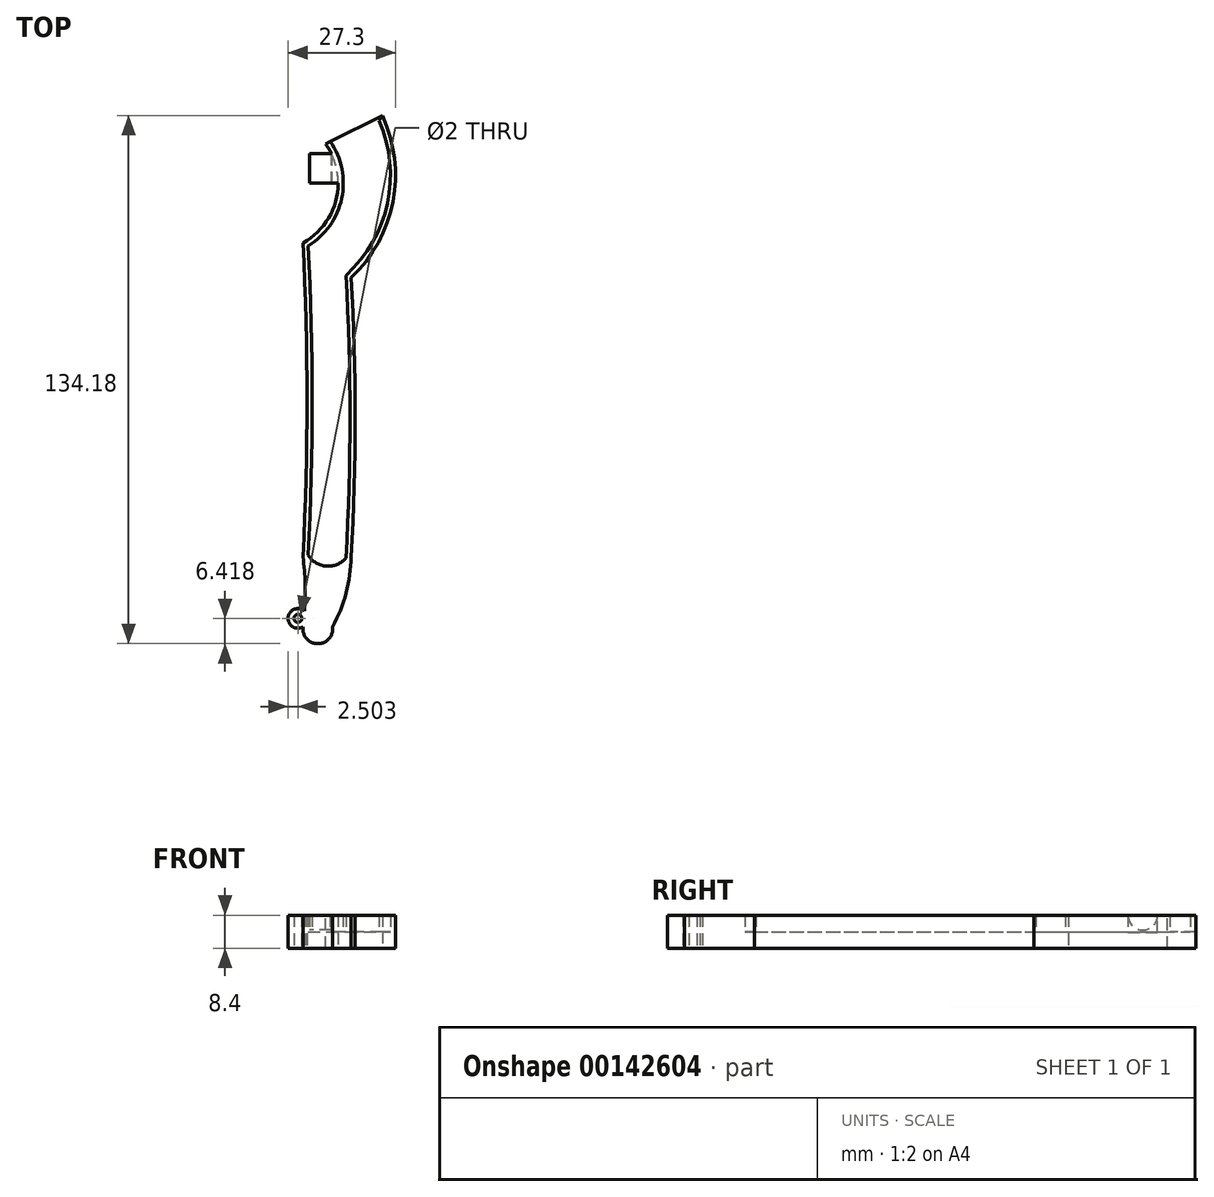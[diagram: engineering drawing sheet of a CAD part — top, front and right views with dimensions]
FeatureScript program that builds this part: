
annotation { "Feature Type Name" : "Feature", "Feature Type Description" : "" }
export const myFeature = defineFeature(function(context is Context, id is Id, definition is map)
    precondition{}
    {
        {
            var Q0;
            Q0=qCreatedBy(makeId("Top.planeOp"),FACE);
            var sketch = newSketch(context, id + "F0", { "sketchPlane" : qUnion([Q0])});
            skArc(sketch, "E0", {"start": v(-18, -31.8) * mm, "mid": v(-9.08, -15.9) * mm, "end": v(-18, 0) * mm});
            skArc(sketch, "E1", {"start": v(-8.38, -39.3) * mm, "mid": v(2.12, -21) * mm, "end": v(0, 0) * mm});
            skArc(sketch, "E2", {"start": v(-18, -110.4) * mm, "mid": v(-17, -71.1) * mm, "end": v(-18, -31.8) * mm});
            skArc(sketch, "E3", {"start": v(-8.38, -111.1) * mm, "mid": v(-7.37, -75.2) * mm, "end": v(-8.38, -39.3) * mm});
            skArc(sketch, "E4", {"start": v(-18, -110.4) * mm, "mid": v(-13.37, -113.18) * mm, "end": v(-8.38, -111.1) * mm});
            skLineSegment(sketch, "E5", {"start": v(0, 0) * mm, "end": v(-18, 0) * mm});
            skArc(sketch, "E6.0", {"start": v(-19.32, -110.8) * mm, "mid": v(-18.3, -70.94) * mm, "end": v(-19.34, -31.07) * mm});
            skLineSegment(sketch, "E6.1", {"start": v(0.84, 1.3) * mm, "end": v(-25.59, 1.3) * mm});
            skArc(sketch, "E6.2", {"start": v(-7.05, -39.84) * mm, "mid": v(3.54, -20.54) * mm, "end": v(0.84, 1.3) * mm});
            skArc(sketch, "E6.3", {"start": v(-19.34, -31.07) * mm, "mid": v(-10.7, -12.62) * mm, "end": v(-25.59, 1.3) * mm});
            skArc(sketch, "E6.4", {"start": v(-7.06, -110.8) * mm, "mid": v(-6.07, -75.32) * mm, "end": v(-7.05, -39.84) * mm});
            skArc(sketch, "E7", {"start": v(-19.32, -128.6) * mm, "mid": v(-18.75, -119.7) * mm, "end": v(-19.32, -110.8) * mm});
            skArc(sketch, "E8", {"start": v(-11.78, -128.6) * mm, "mid": v(-8.38, -119.98) * mm, "end": v(-7.06, -110.8) * mm});
            skArc(sketch, "E9", {"start": v(-19.32, -128.6) * mm, "mid": v(-15.55, -132.88) * mm, "end": v(-11.78, -128.6) * mm});
            skArc(sketch, "E10", {"start": v(-18.93, -124.62) * mm, "mid": v(-23.1, -126.21) * mm, "end": v(-19.32, -128.6) * mm});
            skCircle(sketch, "E11", {"center": v(-20.62, -126.46) * mm, "radius": 1 * mm});
            skLineSegment(sketch, "E12", {"start": v(-10.38, -15.9) * mm, "end": v(-17.68, -15.9) * mm});
            skLineSegment(sketch, "E13", {"start": v(-17.68, -15.9) * mm, "end": v(-17.68, -8.4) * mm});
            skLineSegment(sketch, "E14", {"start": v(-17.68, -8.4) * mm, "end": v(-12.09, -8.4) * mm});
            skSolve(sketch);
        }
        {
            var Q0;
            Q0=makeQuery(id+"F0.imprint","IMPRINT",FACE,{"disambiguationData":[TD([[makeQuery(id+"F0.imprint","IMPRINT",EDGE,{"derivedFrom":sQuery(id+"F0.wireOp",EDGE,"E0")}),1.0]])]});
            var Q1;
            {var subQ0=sQuery(id+"F0.wireOp",EDGE,"E10");Q1=makeQuery(id+"F0.imprint","IMPRINT",FACE,{"disambiguationData":[TD([[makeQuery(id+"F0.imprint","IMPRINT",EDGE,{"derivedFrom":subQ0}),1.0]])]});}
            extrude(context, id + "F1", {"entities" : qUnion([Q0, Q1]), "depth" : 8.4 * mm});
        }
        {
            var Q0;
            Q0=makeQuery(id+"F0.imprint","IMPRINT",FACE,{"disambiguationData":[TD([[makeQuery(id+"F0.imprint","IMPRINT",EDGE,{"derivedFrom":sQuery(id+"F0.wireOp",EDGE,"E0")}),-1.0]])]});
            extrude(context, id + "F2", {"entities" : qUnion([Q0]), "operationType" : NewBodyOperationType.ADD, "depth" : 4.2 * mm});
        }
        {
            var Q0;
            {var subQ0=sQuery(id+"F0.wireOp",EDGE,"E12");Q0=makeQuery(id+"F0.imprint","IMPRINT",FACE,{"disambiguationData":[TD([[makeQuery(id+"F0.imprint","IMPRINT",EDGE,{"derivedFrom":subQ0}),-1.0]])]});}
            extrude(context, id + "F3", {"entities" : qUnion([Q0]), "operationType" : NewBodyOperationType.ADD, "depth" : 8.4 * mm});
        }
        {
            var Q0;
            {var subQ0=sQuery(id+"F0.wireOp",EDGE,"E12");Q0=makeQuery(id+"F0.imprint","IMPRINT",FACE,{"disambiguationData":[TD([[makeQuery(id+"F0.imprint","IMPRINT",EDGE,{"derivedFrom":subQ0}),-1.0]])]});}
            extrude(context, id + "F4", {"entities" : qUnion([Q0]), "operationType" : NewBodyOperationType.REMOVE, "depth" : 4 * mm});
        }
        {
            var Q0;
            Q0=makeQuery(id+"F3.opExtrude","SWEPT_FACE",FACE,{"disambiguationData":[OSD([sQuery(id+"F0.wireOp",EDGE,"E13")])]});
            var sketch = newSketch(context, id + "F5", { "sketchPlane" : qUnion([Q0])});
            skLineSegment(sketch, "E15.0", {"start": v(8.4, 8.4) * mm, "end": v(8.4, 4) * mm});
            skLineSegment(sketch, "E15.1", {"start": v(15.9, 8.4) * mm, "end": v(8.4, 8.4) * mm});
            skLineSegment(sketch, "E15.2", {"start": v(15.9, 8.4) * mm, "end": v(15.9, 4) * mm});
            skLineSegment(sketch, "E15.3", {"start": v(15.9, 4) * mm, "end": v(8.4, 4) * mm});
            skSolve(sketch);
        }
        {
            var Q0;
            {var subQ0=sQuery(id+"F0.wireOp",EDGE,"E6.3");Q0=makeQuery(id+"F3.boolean.opBoolean","MERGE",FACE,{"derivedFrom":[makeQuery(id+"F1.opExtrude","CAP_FACE",FACE,{"disambiguationData":[OSD([sQuery(id+"F0.wireOp",EDGE,"E0"),sQuery(id+"F0.wireOp",EDGE,"E1"),sQuery(id+"F0.wireOp",EDGE,"E2"),sQuery(id+"F0.wireOp",EDGE,"E3"),sQuery(id+"F0.wireOp",EDGE,"E4"),sQuery(id+"F0.wireOp",EDGE,"E5"),sQuery(id+"F0.wireOp",EDGE,"E6.0"),sQuery(id+"F0.wireOp",EDGE,"E6.1"),sQuery(id+"F0.wireOp",EDGE,"E6.2"),subQ0,sQuery(id+"F0.wireOp",EDGE,"E6.4"),sQuery(id+"F0.wireOp",EDGE,"E7"),sQuery(id+"F0.wireOp",EDGE,"E8"),sQuery(id+"F0.wireOp",EDGE,"E9"),sQuery(id+"F0.wireOp",EDGE,"E10"),sQuery(id+"F0.wireOp",EDGE,"E11")])],"isStart":false}),makeQuery(id+"F3.opExtrude","CAP_FACE",FACE,{"disambiguationData":[OSD([subQ0,sQuery(id+"F0.wireOp",EDGE,"E12"),sQuery(id+"F0.wireOp",EDGE,"E13"),sQuery(id+"F0.wireOp",EDGE,"E14")])],"isStart":false})]});}
            var sketch = newSketch(context, id + "F6", { "sketchPlane" : qUnion([Q0])});
            skLineSegment(sketch, "E16.0", {"start": v(0.84, 1.3) * mm, "end": v(-25.59, 1.3) * mm});
            skArc(sketch, "E16.1", {"start": v(-7.05, -39.84) * mm, "mid": v(3.54, -20.54) * mm, "end": v(0.84, 1.3) * mm});
            skArc(sketch, "E16.2", {"start": v(-12.09, -8.4) * mm, "mid": v(-17.6, -1.83) * mm, "end": v(-25.59, 1.3) * mm});
            skLineSegment(sketch, "E16.3", {"start": v(-17.68, -8.4) * mm, "end": v(-12.09, -8.4) * mm});
            skLineSegment(sketch, "E17", {"start": v(0.84, 1.3) * mm, "end": v(-13.56, -5.9) * mm});
            skSolve(sketch);
        }
        {
            var Q0;
            {var subQ1=sQuery(id+"F6.wireOp",EDGE,"E16.0");Q0=makeQuery(id+"F6.imprint","IMPRINT",FACE,{"disambiguationData":[TD([[makeQuery(id+"F6.imprint","IMPRINT",EDGE,{"derivedFrom":subQ1}),1.0]])]});}
            var Q1;
            {var subQ0=sQuery(id+"F6.wireOp",EDGE,"E17");var subQ1=makeQuery(id+"F1.opExtrude","CAP_EDGE",EDGE,{"disambiguationData":[OSD([sQuery(id+"F0.wireOp",EDGE,"E5")])],"isStart":false});var subQ2=makeQuery(id+"F6.imprint","INTERSECT",VERTEX,{"derivedFrom":[subQ1,subQ0]});Q1=makeQuery(id+"F6.imprint","IMPRINT",FACE,{"disambiguationData":[TD([[makeQuery(id+"F6.imprint","IMPRINT",EDGE,{"disambiguationData":[TD([[subQ2,-1.0]])],"derivedFrom":subQ0}),-1.0]])]});}
            extrude(context, id + "F7", {"entities" : qUnion([Q0, Q1]), "operationType" : NewBodyOperationType.REMOVE, "oppositeDirection" : true, "depth" : 25 * mm});
        }
        {
            var Q0;
            {var subQ0=sQuery(id+"F0.wireOp",EDGE,"E6.3");Q0=makeQuery(id+"F3.boolean.opBoolean","MERGE",FACE,{"derivedFrom":[makeQuery(id+"F1.opExtrude","CAP_FACE",FACE,{"disambiguationData":[OSD([sQuery(id+"F0.wireOp",EDGE,"E0"),sQuery(id+"F0.wireOp",EDGE,"E1"),sQuery(id+"F0.wireOp",EDGE,"E2"),sQuery(id+"F0.wireOp",EDGE,"E3"),sQuery(id+"F0.wireOp",EDGE,"E4"),sQuery(id+"F0.wireOp",EDGE,"E5"),sQuery(id+"F0.wireOp",EDGE,"E6.0"),sQuery(id+"F0.wireOp",EDGE,"E6.1"),sQuery(id+"F0.wireOp",EDGE,"E6.2"),subQ0,sQuery(id+"F0.wireOp",EDGE,"E6.4"),sQuery(id+"F0.wireOp",EDGE,"E7"),sQuery(id+"F0.wireOp",EDGE,"E8"),sQuery(id+"F0.wireOp",EDGE,"E9"),sQuery(id+"F0.wireOp",EDGE,"E10"),sQuery(id+"F0.wireOp",EDGE,"E11")])],"isStart":false}),makeQuery(id+"F3.opExtrude","CAP_FACE",FACE,{"disambiguationData":[OSD([subQ0,sQuery(id+"F0.wireOp",EDGE,"E12"),sQuery(id+"F0.wireOp",EDGE,"E13"),sQuery(id+"F0.wireOp",EDGE,"E14")])],"isStart":false})]});}
            var sketch = newSketch(context, id + "F8", { "sketchPlane" : qUnion([Q0])});
            skArc(sketch, "E18.0", {"start": v(-7.05, -39.84) * mm, "mid": v(3.54, -20.54) * mm, "end": v(0.84, 1.3) * mm});
            skLineSegment(sketch, "E18.1", {"start": v(0.84, 1.3) * mm, "end": v(-1.76, 0) * mm});
            skLineSegment(sketch, "E18.2", {"start": v(0, 0) * mm, "end": v(-1.76, 0) * mm});
            skArc(sketch, "E18.3", {"start": v(-8.38, -39.3) * mm, "mid": v(2.12, -21) * mm, "end": v(0, 0) * mm});
            skLineSegment(sketch, "E19", {"start": v(0.84, 1.3) * mm, "end": v(0, 0) * mm});
            skSolve(sketch);
        }
        {
            var Q0;
            Q0=makeQuery(id+"F8.imprint","IMPRINT",FACE,{"disambiguationData":[TD([[makeQuery(id+"F8.imprint","IMPRINT",EDGE,{"derivedFrom":sQuery(id+"F8.wireOp",EDGE,"E18.1")}),1.0]])]});
            extrude(context, id + "F9", {"entities" : qUnion([Q0]), "operationType" : NewBodyOperationType.REMOVE, "oppositeDirection" : true, "depth" : 4.2 * mm});
        }
        {
            var Q0;
            Q0=makeQuery(id+"F5.imprint","IMPRINT",FACE,{"disambiguationData":[TD([[makeQuery(id+"F5.imprint","IMPRINT",EDGE,{"derivedFrom":sQuery(id+"F5.wireOp",EDGE,"E15.0")}),1.0]])]});
            var sketch = newSketch(context, id + "F10", { "sketchPlane" : qUnion([Q0])});
            skLineSegment(sketch, "E20.0", {"start": v(15.9, 8.4) * mm, "end": v(8.4, 8.4) * mm});
            skLineSegment(sketch, "E20.1", {"start": v(8.4, 8.4) * mm, "end": v(8.4, 4) * mm});
            skLineSegment(sketch, "E20.2", {"start": v(15.9, 4) * mm, "end": v(8.4, 4) * mm});
            skLineSegment(sketch, "E20.3", {"start": v(15.9, 8.4) * mm, "end": v(15.9, 4) * mm});
            skArc(sketch, "E21", {"start": v(8.4, 8.4) * mm, "mid": v(12.15, 4.65) * mm, "end": v(15.9, 8.4) * mm});
            skSolve(sketch);
        }
        {
            var Q0;
            Q0=makeQuery(id+"F10.imprint","IMPRINT",FACE,{"disambiguationData":[TD([[makeQuery(id+"F10.imprint","IMPRINT",EDGE,{"derivedFrom":sQuery(id+"F10.wireOp",EDGE,"E20.2")}),-1.0]])]});
            extrude(context, id + "F11", {"entities" : qUnion([Q0]), "operationType" : NewBodyOperationType.REMOVE, "oppositeDirection" : true, "depth" : 5.6 * mm});
        }
    });
